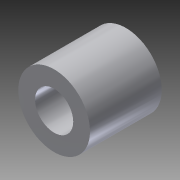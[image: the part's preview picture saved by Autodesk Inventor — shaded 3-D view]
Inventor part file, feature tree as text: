
AUTODESK INVENTOR PART (.ipt)
format: ipt  version: 2014 SP1 (Build 180222100, 222)  size: 82,944 bytes
history: native  units: in
note: dims shown in document units (in); Inventor stores cm internally (conversion verified against a paired STEP export)
features: extrude x1, sketch x1
ambient origin geometry x8: Origin, YZ Plane, XZ Plane, XY Plane, X Axis, Y Axis, Z Axis, Center Point
bodies: Solid1 (feature_tree)
feature tree (2):
  extrude  "Extrusion1"  Depth=0.5in
  sketch  "Sketch1"  dims[d0=0.266in d1=0.5in d2=0.5in d3=0.0in]
